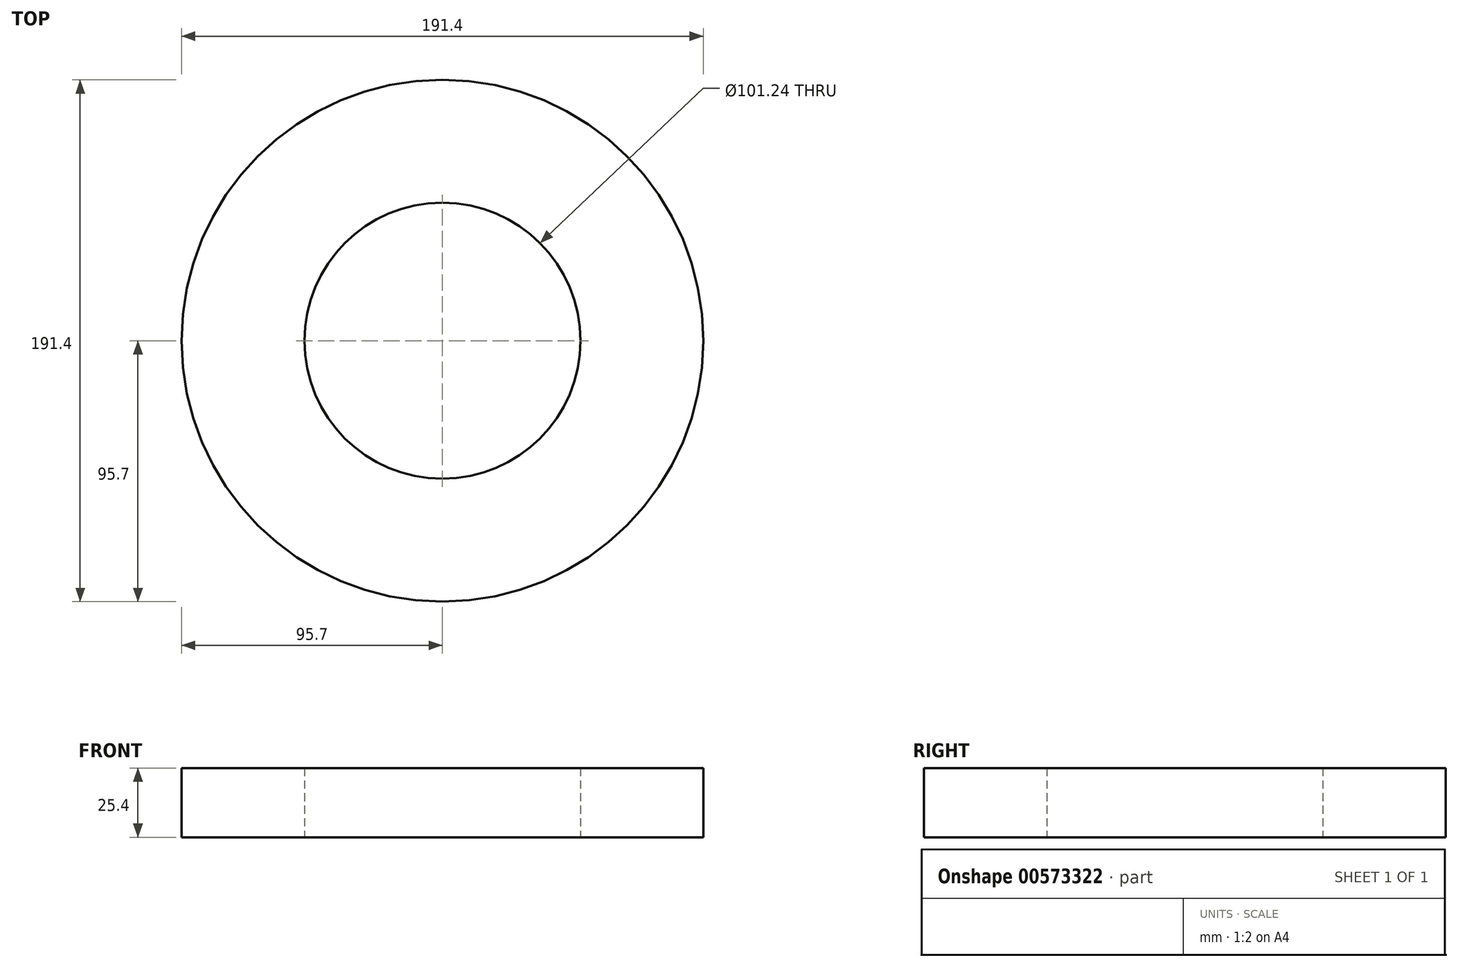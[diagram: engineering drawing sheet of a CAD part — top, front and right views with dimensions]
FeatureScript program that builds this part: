
annotation { "Feature Type Name" : "Feature", "Feature Type Description" : "" }
export const myFeature = defineFeature(function(context is Context, id is Id, definition is map)
    precondition{}
    {
        {
            var Q0;
            Q0=qCreatedBy(makeId("Top.planeOp"),FACE);
            var sketch = newSketch(context, id + "F0", { "sketchPlane" : qUnion([Q0])});
            skCircle(sketch, "E0", {"center": v(0, 0) * mm, "radius": 50.62 * mm});
            skCircle(sketch, "E1", {"center": v(0, 0) * mm, "radius": 95.7 * mm});
            skSolve(sketch);
        }
        {
            var Q0;
            Q0 = qSketchRegion(id + "F0", true);
            extrude(context, id + "F1", {"entities" : qUnion([Q0]), "depth" : 25.4 * mm, "offsetDistance" : 25.4 * mm});
        }
    });
